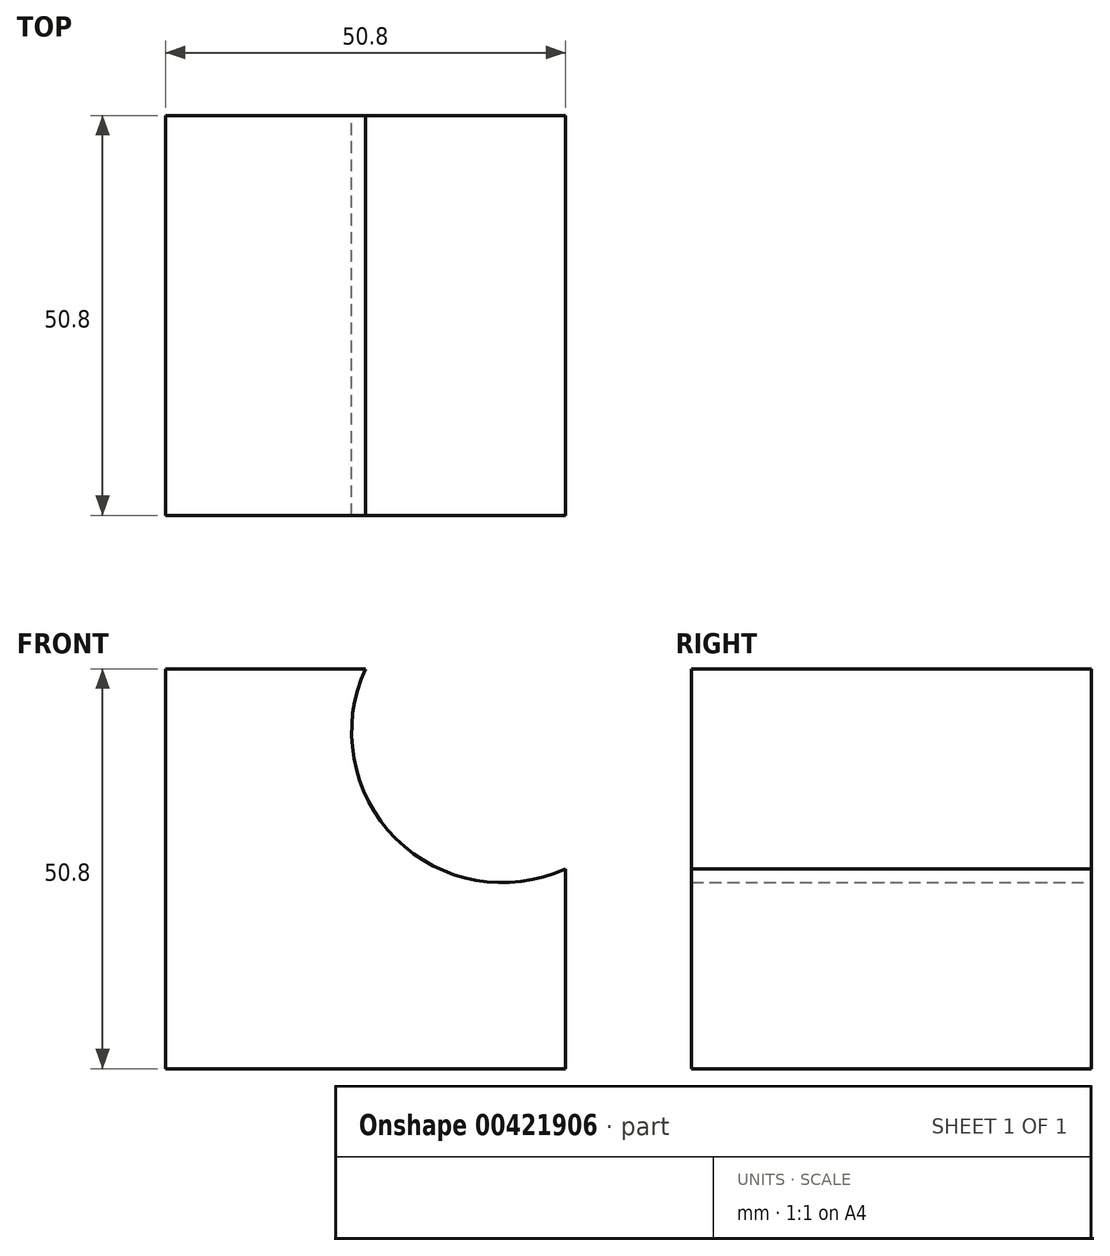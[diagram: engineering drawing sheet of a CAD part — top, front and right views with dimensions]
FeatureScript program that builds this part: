
annotation { "Feature Type Name" : "Feature", "Feature Type Description" : "" }
export const myFeature = defineFeature(function(context is Context, id is Id, definition is map)
    precondition{}
    {
        {
            var Q0;
            Q0=qCreatedBy(makeId("Front.planeOp"),FACE);
            var sketch = newSketch(context, id + "F0", { "sketchPlane" : qUnion([Q0])});
            skLineSegment(sketch, "E0", {"start": v(0, 0) * mm, "end": v(-50.8, 0) * mm});
            skLineSegment(sketch, "E1", {"start": v(-50.8, 0) * mm, "end": v(-50.8, 50.8) * mm});
            skLineSegment(sketch, "E2", {"start": v(-50.8, 50.8) * mm, "end": v(-25.4, 50.8) * mm});
            skLineSegment(sketch, "E3", {"start": v(0, 0) * mm, "end": v(0, 25.4) * mm});
            skArc(sketch, "E4", {"start": v(-25.4, 50.8) * mm, "mid": v(-21.56, 29.24) * mm, "end": v(0, 25.4) * mm});
            skSolve(sketch);
        }
        {
            var Q0;
            Q0=makeQuery(id+"F0.imprint","IMPRINT",FACE,{"disambiguationData":[TD([[makeQuery(id+"F0.imprint","IMPRINT",EDGE,{"derivedFrom":sQuery(id+"F0.wireOp",EDGE,"E0")}),-1.0]])]});
            extrude(context, id + "F1", {"entities" : qUnion([Q0]), "depth" : 50.8 * mm});
        }
    });
